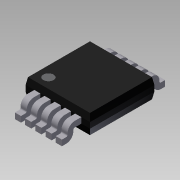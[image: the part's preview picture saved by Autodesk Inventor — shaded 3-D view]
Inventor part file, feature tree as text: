
AUTODESK INVENTOR PART (.ipt)
format: ipt  version: 2011 (Build 150239000, 239)  size: 294,912 bytes
history: native  units: mm
features: extrude x5, sketch x5, projected_geometry x5, other x3, mirror x1, pattern_linear x1
ambient origin geometry x8: Origin, YZ Plane, XZ Plane, XY Plane, X Axis, Y Axis, Z Axis, Center Point
feature tree (20):
  other  "Твердое тело1"
  extrude  "Выдавливание1"  Depth=1.575mm
  extrude  "Выдавливание2"  Depth=1.575mm
  extrude  "Выдавливание3"  Depth=3.15mm
  other  "РабПлоскость1"
  extrude  "Выдавливание4"  Depth=3.15mm
  other  "РабПлоскость2"
  mirror  "Зеркальное отражение1"
  pattern_linear  "Прямоуг.массив1"  Spacing1=1.09mm  [1 undecoded]
  extrude  "Выдавливание5"  Depth=0.28mm
  sketch  "Эскиз1"
  sketch  "Эскиз2"
  sketch  "Эскиз3"
  projected_geometry  "Спроецированная петля1"
  projected_geometry  "Спроецированная петля2"
  sketch  "Эскиз4"
  projected_geometry  "Спроецированная петля3"
  projected_geometry  "Спроецированная петля4"
  projected_geometry  "Спроецированная петля5"
  sketch  "Эскиз5"
note: 1 required parameter value undecoded (feature->parameter linkage not recoverable at this tier; creation-order binding heuristic only, values carry confidence <= 0.55)
